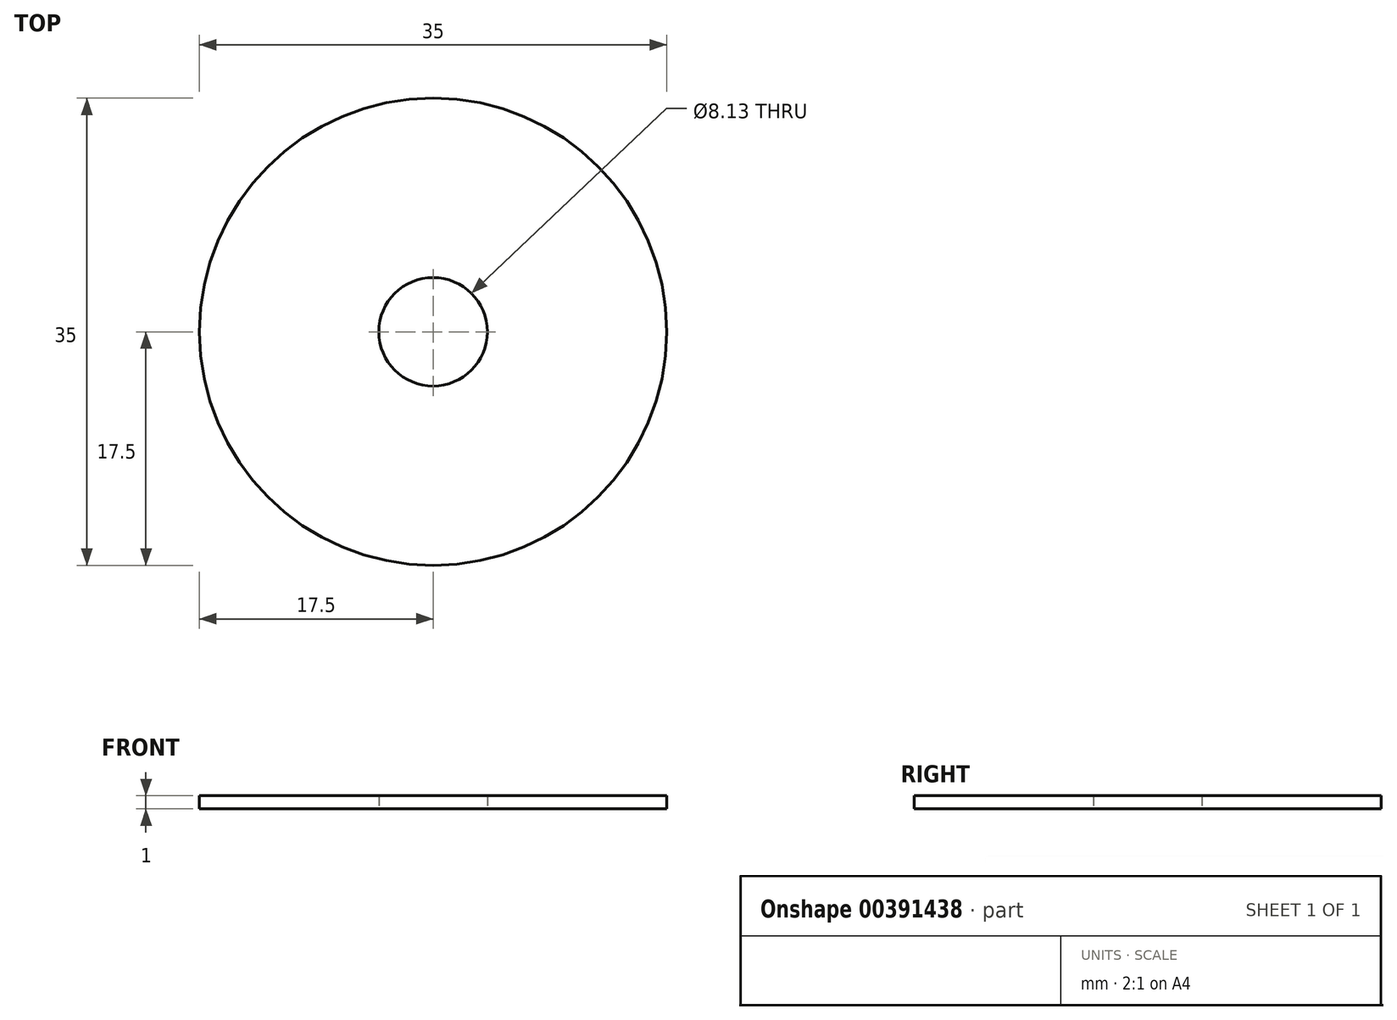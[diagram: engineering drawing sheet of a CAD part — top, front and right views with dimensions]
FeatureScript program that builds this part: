
annotation { "Feature Type Name" : "Feature", "Feature Type Description" : "" }
export const myFeature = defineFeature(function(context is Context, id is Id, definition is map)
    precondition{}
    {
        {
            var Q0;
            Q0=qCreatedBy(makeId("Front.planeOp"),FACE);
            var sketch = newSketch(context, id + "F0", { "sketchPlane" : qUnion([Q0])});
            skLineSegment(sketch, "E0", {"start": v(0, 0) * mm, "end": v(0, 10) * mm, "construction": true});
            skLineSegment(sketch, "E1.bottom", {"start": v(-4.06, 0) * mm, "end": v(-17.5, 0) * mm});
            skLineSegment(sketch, "E1.top", {"start": v(-4.06, 1) * mm, "end": v(-17.5, 1) * mm});
            skLineSegment(sketch, "E1.left", {"start": v(-4.06, 0) * mm, "end": v(-4.06, 1) * mm});
            skLineSegment(sketch, "E1.right", {"start": v(-17.5, 0) * mm, "end": v(-17.5, 1) * mm});
            skSolve(sketch);
        }
        {
            var Q0;
            Q0=qSketchRegion(id+"F0",true);
            var Q1;
            Q1=sQuery(id+"F0.wireOp",EDGE,"E0");
            revolve(context, id + "F1", {"entities" : qUnion([Q0]), "axis" : qUnion([Q1]), "revolveType" : RevolveType.FULL});
        }
    });
